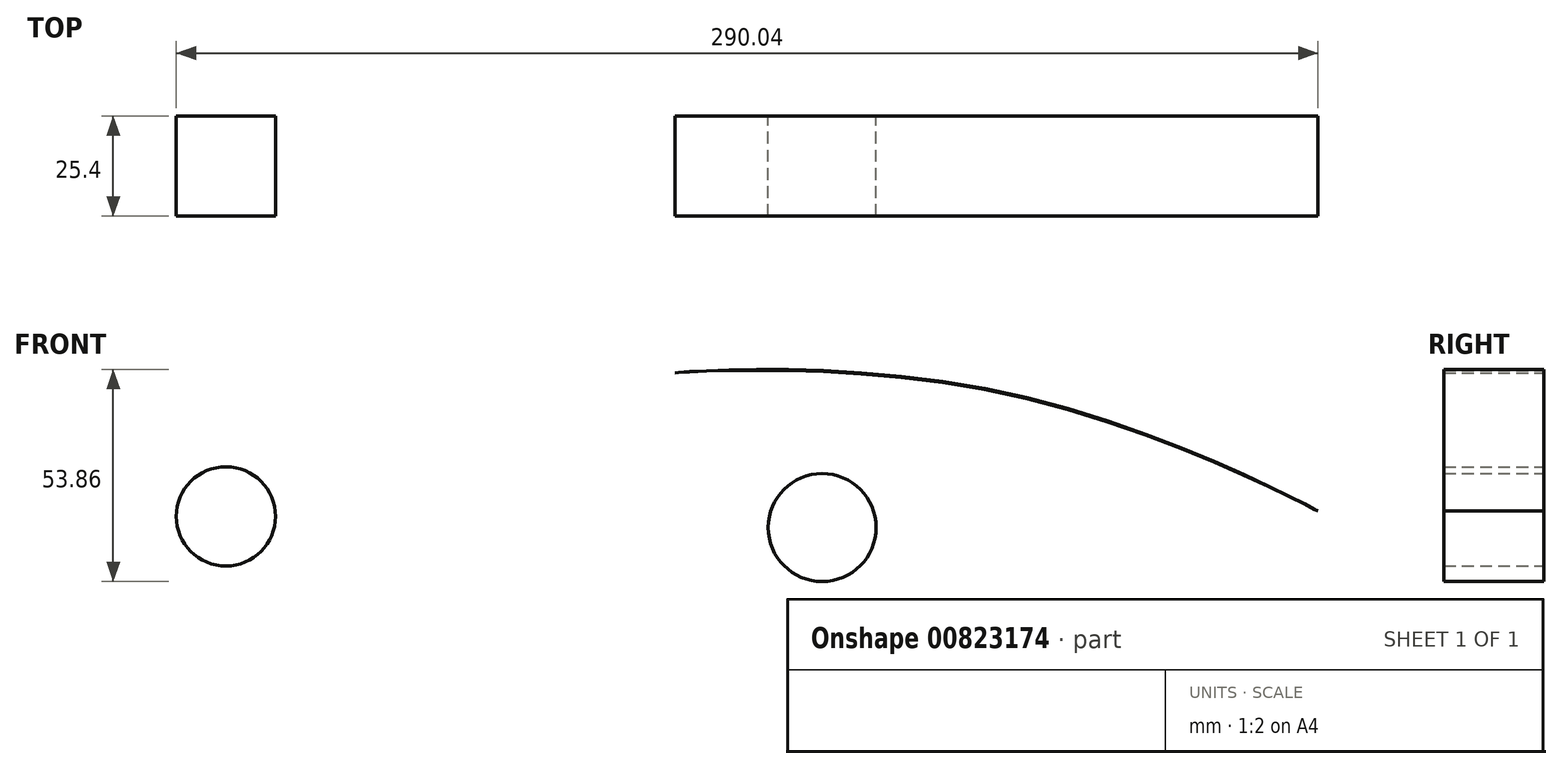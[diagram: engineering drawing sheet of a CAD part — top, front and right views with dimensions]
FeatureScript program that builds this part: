
annotation { "Feature Type Name" : "Feature", "Feature Type Description" : "" }
export const myFeature = defineFeature(function(context is Context, id is Id, definition is map)
    precondition{}
    {
        {
            var Q0;
            Q0=qCreatedBy(makeId("Front.planeOp"),FACE);
            var sketch = newSketch(context, id + "F0", { "sketchPlane" : qUnion([Q0])});
            skFitSpline(sketch, "E0", {"points": [v(92.92, -11) * mm, v(12.81, 19.22) * mm, v(-70.46, 24.14) * mm, v(13.16, 18.87) * mm, v(92.92, -11) * mm]});
            skLineSegment(sketch, "E1", {"start": v(92.92, -11) * mm, "end": v(-16, -11) * mm});
            skArc(sketch, "E2", {"start": v(-16, -11) * mm, "mid": v(-33.04, 2.36) * mm, "end": v(-50.08, -11) * mm});
            skLineSegment(sketch, "E3", {"start": v(-50.08, -11) * mm, "end": v(-154.78, -11) * mm});
            skCircle(sketch, "E4", {"center": v(-33.04, -15.18) * mm, "radius": 13.71 * mm});
            skArc(sketch, "E5", {"start": v(-70.46, 24.14) * mm, "mid": v(-121.08, 47.64) * mm, "end": v(-171.7, 24.14) * mm});
            skLineSegment(sketch, "E6", {"start": v(-154.78, -11) * mm, "end": v(-169.1, -11) * mm});
            skArc(sketch, "E7", {"start": v(-169.1, -11) * mm, "mid": v(-184.5, 3.1) * mm, "end": v(-199.9, -11) * mm});
            skLineSegment(sketch, "E8", {"start": v(-199.9, -11) * mm, "end": v(-208.97, -11) * mm});
            skLineSegment(sketch, "E9", {"start": v(-208.97, -11) * mm, "end": v(-208.97, 28.95) * mm});
            skArc(sketch, "E10", {"start": v(-171.7, 24.14) * mm, "mid": v(-189.77, 30.94) * mm, "end": v(-208.97, 28.95) * mm});
            skCircle(sketch, "E11", {"center": v(-184.5, -12.35) * mm, "radius": 12.61 * mm});
            skLineSegment(sketch, "E12", {"start": v(-81.25, 22) * mm, "end": v(-81.25, -3.96) * mm});
            skLineSegment(sketch, "E13", {"start": v(-81.25, -3.96) * mm, "end": v(-107.21, -3.96) * mm});
            skLineSegment(sketch, "E14", {"start": v(-107.21, -3.96) * mm, "end": v(-107.21, 37.4) * mm});
            skArc(sketch, "E15", {"start": v(-81.25, 22) * mm, "mid": v(-92.02, 33.44) * mm, "end": v(-107.21, 37.4) * mm});
            skLineSegment(sketch, "E16", {"start": v(-87.89, 18.68) * mm, "end": v(-103.29, 18.68) * mm});
            skLineSegment(sketch, "E17", {"start": v(-103.29, 18.68) * mm, "end": v(-103.29, 31.37) * mm});
            skArc(sketch, "E18", {"start": v(-87.89, 18.68) * mm, "mid": v(-93.26, 27.85) * mm, "end": v(-103.29, 31.37) * mm});
            skCircle(sketch, "E19", {"center": v(-102.08, 10.83) * mm, "radius": 2.3 * mm});
            skSolve(sketch);
        }
        {
            var Q0;
            Q0=makeQuery(id+"F0.imprint","IMPRINT",FACE,{"disambiguationData":[TD([[makeQuery(id+"F0.imprint","IMPRINT",EDGE,{"derivedFrom":sQuery(id+"F0.wireOp",EDGE,"E4")}),1.0]])]});
            var Q1;
            {var subQ1=sQuery(id+"F0.wireOp",EDGE,"E1");Q1=makeQuery(id+"F0.imprint","IMPRINT",FACE,{"disambiguationData":[TD([[makeQuery(id+"F0.imprint","IMPRINT",EDGE,{"derivedFrom":subQ1}),-1.0]])]});}
            var Q2;
            Q2=makeQuery(id+"F0.imprint","IMPRINT",FACE,{"disambiguationData":[TD([[makeQuery(id+"F0.imprint","IMPRINT",EDGE,{"derivedFrom":sQuery(id+"F0.wireOp",EDGE,"E11")}),1.0]])]});
            extrude(context, id + "F1", {"entities" : qUnion([Q0, Q1, Q2]), "depth" : 25.4 * mm, "offsetDistance" : 25.4 * mm});
        }
        {
            var Q0;
            Q0=makeQuery(id+"F1.opExtrude","CAP_FACE",FACE,{"disambiguationData":[OSD([sQuery(id+"F0.wireOp",EDGE,"E0"),sQuery(id+"F0.wireOp",EDGE,"E1"),sQuery(id+"F0.wireOp",EDGE,"E2"),sQuery(id+"F0.wireOp",EDGE,"E3"),sQuery(id+"F0.wireOp",EDGE,"E5"),sQuery(id+"F0.wireOp",EDGE,"E6"),sQuery(id+"F0.wireOp",EDGE,"E7"),sQuery(id+"F0.wireOp",EDGE,"E8"),sQuery(id+"F0.wireOp",EDGE,"E9"),sQuery(id+"F0.wireOp",EDGE,"E10"),sQuery(id+"F0.wireOp",EDGE,"E12"),sQuery(id+"F0.wireOp",EDGE,"E13"),sQuery(id+"F0.wireOp",EDGE,"E14"),sQuery(id+"F0.wireOp",EDGE,"E15")])],"isStart":true});
            var sketch = newSketch(context, id + "F2", { "sketchPlane" : qUnion([Q0])});
            skLineSegment(sketch, "E20", {"start": v(86.38, 18.08) * mm, "end": v(102.08, 18.08) * mm});
            skLineSegment(sketch, "E21", {"start": v(102.08, 18.08) * mm, "end": v(102.08, 29.55) * mm});
            skArc(sketch, "E22", {"start": v(102.08, 29.55) * mm, "mid": v(92.48, 26.21) * mm, "end": v(86.38, 18.08) * mm});
            skCircle(sketch, "E23", {"center": v(102.74, 12.16) * mm, "radius": 2.55 * mm});
            skSolve(sketch);
        }
        {
            var Q0;
            Q0=makeQuery(id+"F2.imprint","IMPRINT",FACE,{"disambiguationData":[TD([[makeQuery(id+"F2.imprint","IMPRINT",EDGE,{"derivedFrom":sQuery(id+"F2.wireOp",EDGE,"E20")}),1.0]])]});
            var sketch = newSketch(context, id + "F3", { "sketchPlane" : qUnion([Q0])});
            skSolve(sketch);
        }
        {
            var Q0;
            Q0=makeQuery(id+"F3.imprint","IMPRINT",FACE,{"disambiguationData":[TD([[makeQuery(id+"F3.imprint","IMPRINT",EDGE,{"derivedFrom":makeQuery(id+"F2.imprint","IMPRINT",EDGE,{"derivedFrom":sQuery(id+"F2.wireOp",EDGE,"E20")})}),1.0]])]});
            var Q1;
            Q1=makeQuery(id+"F2.imprint","IMPRINT",FACE,{"disambiguationData":[TD([[makeQuery(id+"F2.imprint","IMPRINT",EDGE,{"derivedFrom":sQuery(id+"F2.wireOp",EDGE,"E20")}),1.0]])]});
            var Q2;
            Q2=makeQuery(id+"F2.imprint","IMPRINT",FACE,{"disambiguationData":[TD([[makeQuery(id+"F2.imprint","IMPRINT",EDGE,{"derivedFrom":sQuery(id+"F2.wireOp",EDGE,"E23")}),1.0]])]});
            extrude(context, id + "F4", {"entities" : qUnion([Q0, Q1, Q2]), "depth" : 2.54 * mm, "offsetDistance" : 25.4 * mm});
        }
        {
            var Q0;
            {var subQ0=sQuery(id+"F2.wireOp",EDGE,"E22");var subQ1=sQuery(id+"F2.wireOp",EDGE,"E21");var subQ2=sQuery(id+"F2.wireOp",EDGE,"E20");Q0=makeQuery(id+"F4.opExtrude","SWEPT_BODY",BODY,{"disambiguationData":[OSD([subQ2,subQ1,subQ0]),TDD([makeQuery(id+"F2.imprint","IMPRINT",EDGE,{"derivedFrom":subQ2}),makeQuery(id+"F2.imprint","IMPRINT",EDGE,{"derivedFrom":subQ1}),makeQuery(id+"F2.imprint","IMPRINT",EDGE,{"derivedFrom":subQ0})])]});}
            var Q1;
            Q1=makeQuery(id+"F4.opExtrude","SWEPT_BODY",BODY,{"disambiguationData":[OSD([sQuery(id+"F2.wireOp",EDGE,"E23")])]});
            deleteBodies(context, id + "F5", {"entities" : qUnion([Q0, Q1])});
        }
        {
            var Q0;
            {var subQ0=sQuery(id+"F2.wireOp",EDGE,"E22");var subQ1=sQuery(id+"F2.wireOp",EDGE,"E21");var subQ2=sQuery(id+"F2.wireOp",EDGE,"E20");Q0=makeQuery(id+"F4.opExtrude","SWEPT_BODY",BODY,{"disambiguationData":[OSD([subQ2,subQ1,subQ0]),TDD([makeQuery(id+"F3.imprint","IMPRINT",EDGE,{"derivedFrom":makeQuery(id+"F2.imprint","IMPRINT",EDGE,{"derivedFrom":subQ2})}),makeQuery(id+"F3.imprint","IMPRINT",EDGE,{"derivedFrom":makeQuery(id+"F2.imprint","IMPRINT",EDGE,{"derivedFrom":subQ1})}),makeQuery(id+"F3.imprint","IMPRINT",EDGE,{"derivedFrom":makeQuery(id+"F2.imprint","IMPRINT",EDGE,{"derivedFrom":subQ0})})])]});}
            deleteBodies(context, id + "F6", {"entities" : qUnion([Q0])});
        }
    });
